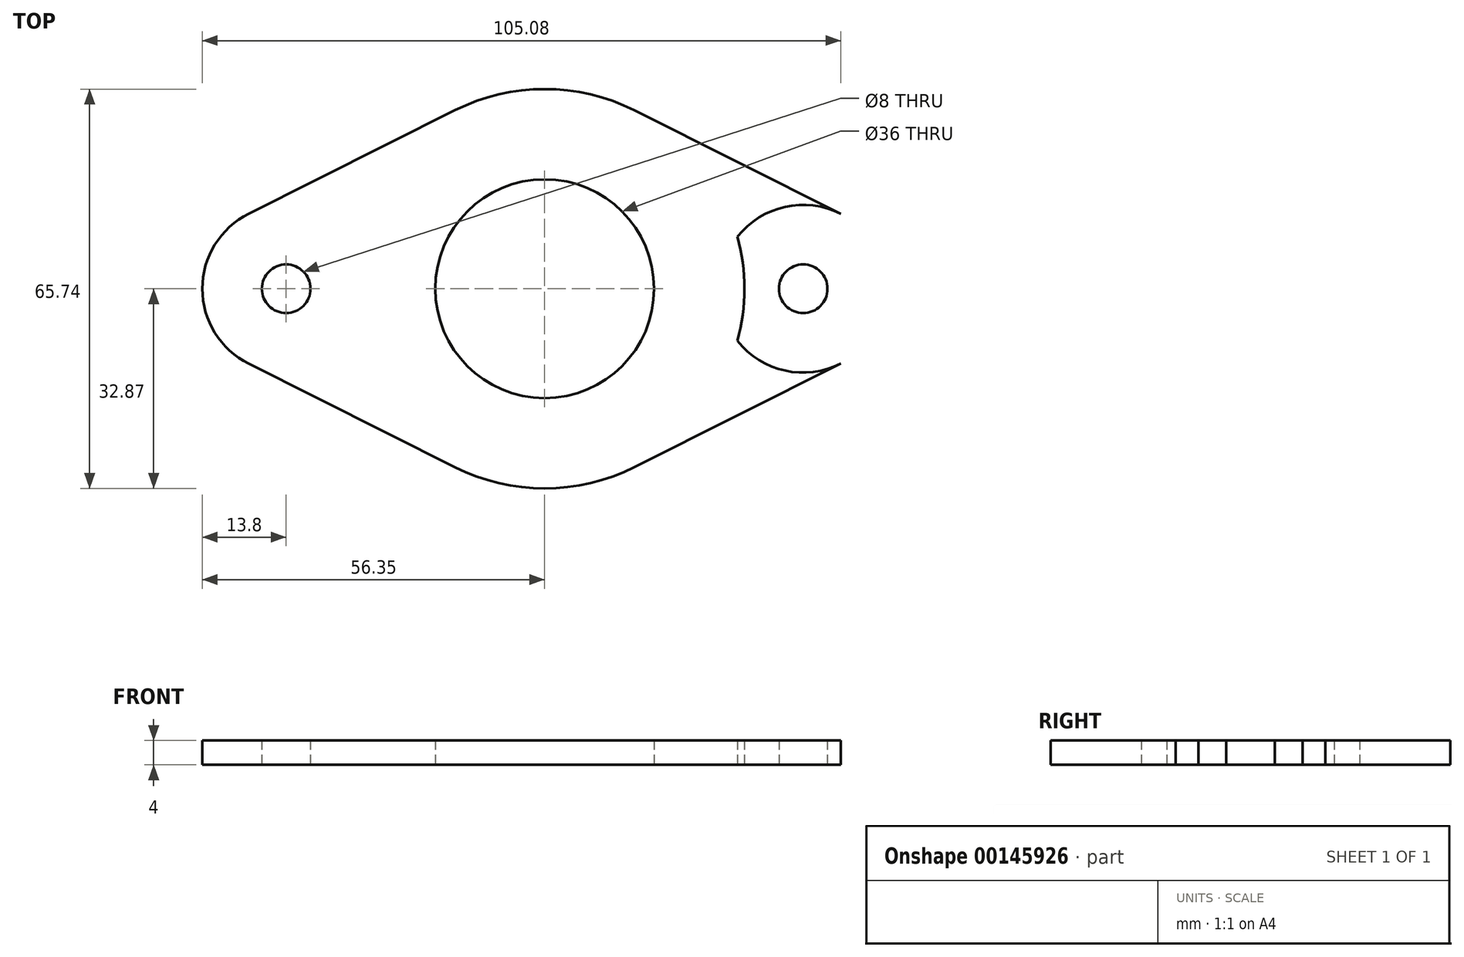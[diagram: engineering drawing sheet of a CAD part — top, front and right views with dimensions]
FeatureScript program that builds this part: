
annotation { "Feature Type Name" : "Feature", "Feature Type Description" : "" }
export const myFeature = defineFeature(function(context is Context, id is Id, definition is map)
    precondition{}
    {
        {
            var Q0;
            Q0=qCreatedBy(makeId("Top.planeOp"),FACE);
            var sketch = newSketch(context, id + "F0", { "sketchPlane" : qUnion([Q0])});
            skPoint(sketch, "E0", {"position": v(-56.35, 0) * mm});
            skPoint(sketch, "E1.MirrorP", {"position": v(56.35, 0) * mm});
            skLineSegment(sketch, "E2", {"start": v(-48.73, 12.34) * mm, "end": v(-14.73, 29.38) * mm});
            skPoint(sketch, "E3", {"position": v(0, 32.88) * mm});
            skPoint(sketch, "E4.MirrorP", {"position": v(0, -32.88) * mm});
            skCircle(sketch, "E5", {"center": v(0, 0) * mm, "radius": 18 * mm});
            skCircle(sketch, "E6", {"center": v(-42.55, 0) * mm, "radius": 4 * mm});
            skCircle(sketch, "E7.0", {"center": v(-42.55, 0) * mm, "radius": 13.8 * mm});
            skCircle(sketch, "E8", {"center": v(0, 0) * mm, "radius": 32.87 * mm});
            skLineSegment(sketch, "E9.MirrorCS", {"start": v(-48.73, -12.34) * mm, "end": v(-14.73, -29.38) * mm});
            skPoint(sketch, "E10.orphan", {"position": v(57.65, 7.87) * mm});
            skPoint(sketch, "E11.MirrorCS.end.orphan", {"position": v(0, 36.77) * mm});
            skCircle(sketch, "E12.MirrorC", {"center": v(42.55, 0) * mm, "radius": 13.8 * mm});
            skCircle(sketch, "E13.MirrorC", {"center": v(42.55, 0) * mm, "radius": 4 * mm});
            skLineSegment(sketch, "E14.MirrorCS", {"start": v(48.73, 12.34) * mm, "end": v(14.73, 29.38) * mm});
            skLineSegment(sketch, "E15.MirrorCS", {"start": v(48.73, -12.34) * mm, "end": v(14.73, -29.38) * mm});
            skPoint(sketch, "E16.orphan", {"position": v(-57.65, 7.87) * mm});
            skPoint(sketch, "E17.orphan", {"position": v(-57.65, -7.87) * mm});
            skPoint(sketch, "E18.orphan", {"position": v(0, -36.77) * mm});
            skPoint(sketch, "E19.orphan", {"position": v(57.65, -7.87) * mm});
            skSolve(sketch);
        }
        {
            var Q0;
            Q0=makeQuery(id+"F0.imprint","IMPRINT",FACE,{"disambiguationData":[TD([[makeQuery(id+"F0.imprint","IMPRINT",EDGE,{"derivedFrom":sQuery(id+"F0.wireOp",EDGE,"E6")}),-1.0]])]});
            var Q1;
            {var subQ0=sQuery(id+"F0.wireOp",EDGE,"E8");var subQ1=sQuery(id+"F0.wireOp",EDGE,"E7.0");var subQ2=makeQuery(id+"F0.imprint","INTERSECT",VERTEX,{"disambiguationData":[OD(0.0)],"derivedFrom":[subQ1,subQ0]});Q1=makeQuery(id+"F0.imprint","IMPRINT",FACE,{"disambiguationData":[TD([[makeQuery(id+"F0.imprint","IMPRINT",EDGE,{"disambiguationData":[TD([[subQ2,1.0]])],"derivedFrom":subQ1}),1.0]])]});}
            var Q2;
            Q2=makeQuery(id+"F0.imprint","IMPRINT",FACE,{"disambiguationData":[TD([[makeQuery(id+"F0.imprint","IMPRINT",EDGE,{"derivedFrom":sQuery(id+"F0.wireOp",EDGE,"E5")}),-1.0]])]});
            var Q3;
            {var subQ0=sQuery(id+"F0.wireOp",EDGE,"E2");Q3=makeQuery(id+"F0.imprint","IMPRINT",FACE,{"disambiguationData":[TD([[makeQuery(id+"F0.imprint","IMPRINT",EDGE,{"derivedFrom":subQ0}),-1.0]])]});}
            var Q4;
            {var subQ0=sQuery(id+"F0.wireOp",EDGE,"E9.MirrorCS");Q4=makeQuery(id+"F0.imprint","IMPRINT",FACE,{"disambiguationData":[TD([[makeQuery(id+"F0.imprint","IMPRINT",EDGE,{"derivedFrom":subQ0}),1.0]])]});}
            var Q5;
            {var subQ0=sQuery(id+"F0.wireOp",EDGE,"E12.MirrorC");var subQ1=sQuery(id+"F0.wireOp",EDGE,"E8");var subQ2=makeQuery(id+"F0.imprint","INTERSECT",VERTEX,{"disambiguationData":[OD(0.0)],"derivedFrom":[subQ1,subQ0]});Q5=makeQuery(id+"F0.imprint","IMPRINT",FACE,{"disambiguationData":[TD([[makeQuery(id+"F0.imprint","IMPRINT",EDGE,{"disambiguationData":[TD([[subQ2,1.0]])],"derivedFrom":subQ1}),1.0]])]});}
            var Q6;
            {var subQ0=sQuery(id+"F0.wireOp",EDGE,"E15.MirrorCS");Q6=makeQuery(id+"F0.imprint","IMPRINT",FACE,{"disambiguationData":[TD([[makeQuery(id+"F0.imprint","IMPRINT",EDGE,{"derivedFrom":subQ0}),-1.0]])]});}
            var Q7;
            Q7=makeQuery(id+"F0.imprint","IMPRINT",FACE,{"disambiguationData":[TD([[makeQuery(id+"F0.imprint","IMPRINT",EDGE,{"derivedFrom":sQuery(id+"F0.wireOp",EDGE,"E13.MirrorC")}),1.0]])]});
            var Q8;
            {var subQ0=sQuery(id+"F0.wireOp",EDGE,"E14.MirrorCS");Q8=makeQuery(id+"F0.imprint","IMPRINT",FACE,{"disambiguationData":[TD([[makeQuery(id+"F0.imprint","IMPRINT",EDGE,{"derivedFrom":subQ0}),1.0]])]});}
            extrude(context, id + "F1", {"entities" : qUnion([Q0, Q1, Q2, Q3, Q4, Q5, Q6, Q7, Q8]), "endBound" : BoundingType.SYMMETRIC, "depth" : 4 * mm});
        }
    });
